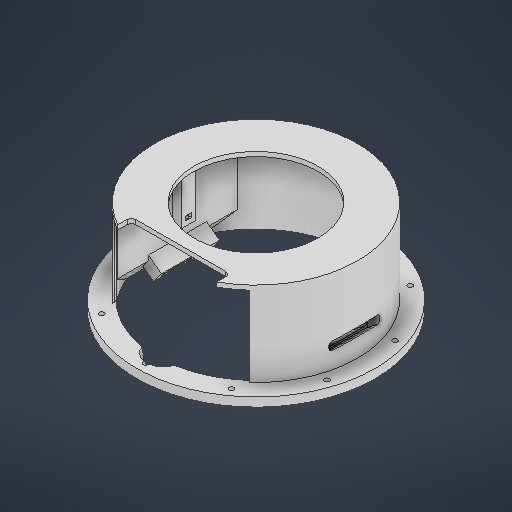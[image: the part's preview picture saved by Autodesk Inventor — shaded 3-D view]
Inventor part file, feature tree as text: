
AUTODESK INVENTOR PART (.ipt)
format: ipt  version: 2025 (Build 290162000, 162)  size: 523,264 bytes
history: native  units: in
note: dims shown in document units (in); Inventor stores cm internally (conversion verified against a paired STEP export)
features: extrude x17, sketch x15, plane x3, fillet x1, chamfer x1
ambient origin geometry x8: Origin, YZ Plane, XZ Plane, XY Plane, X Axis, Y Axis, Z Axis, Center Point
bodies: Solid1 (feature_tree)
feature tree (37):
  sketch  "Sketch1"  dims[d5=0.0in d7=0.0in]
  extrude  "Extrusion1"  TaperAngle=0.0deg  [1 undecoded]
  extrude  "Extrusion2"  Depth=4.5276in
  extrude  "Extrusion7"  Depth=0.2165in
  extrude  "Extrusion34"  Depth=6.1024in
  sketch  "Sketch30"  dims[d272=3.937in d273=4.1535in d274=0.0in d285=3.937in]
  plane  "Work Plane19"
  plane  "Work Plane21"
  plane  "Work Plane22"
  extrude  "Extrusion36"  Depth=4.1535in TaperAngle=0.0deg
  fillet  "Fillet19"  Radius=3.937in
  extrude  "Extrusion37"  Depth=2.0812in TaperAngle=0.0deg
  extrude  "Extrusion38"  Depth=0.1969in
  sketch  "Sketch35"  dims[d293=0.1969in d294=0.1969in]
  extrude  "Extrusion40"  Depth=1.5748in
  extrude  "Extrusion41"  Depth=0.1969in
  extrude  "Extrusion42"  Depth=0.3937in TaperAngle=0.0deg
  extrude  "Extrusion43"  Depth=1.7717in TaperAngle=0.0deg
  chamfer  "Chamfer14"  Distance=0.5906in
  sketch  "Sketch38"  dims[d301=2.9528in]
  extrude  "Extrusion44"  Depth=0.0689in
  extrude  "Extrusion45"  Depth=0.0689in TaperAngle=0.0deg
  sketch  "Sketch39"  dims[d308=6.378in]
  extrude  "Extrusion46"  Depth=0.0689in TaperAngle=0.0deg
  extrude  "Extrusion47"  Depth=0.0689in TaperAngle=0.0deg
  sketch  "Sketch43"  dims[d312=6.8898in d313=5.5413in d314=0.2362in d315=0.1969in d316=0.0in d317=0.1969in d318=0.0in d319=1.378in d320=0.0in d321=0.5906in d322=0.7874in d323=45.0deg d324=1.0in d326=0.315in d328=0.0in d329=0.0in d330=0.1772in d331=0.315in d332=0.0in d333=1.0in d334=0.2953in d335=0.1772in d336=0.0in d337=0.0in d338=0.315in d339=0.0in d340=0.8661in d341=0.8661in d344=0.5906in d345=0.5906in d346=0.5906in d347=0.5906in d348=0.5906in d349=0.0in d350=0.1969in d351=0.0in d352=0.5906in d353=0.5906in d354=0.5906in d355=0.5906in d356=0.5906in d357=0.1969in d358=0.0in d359=0.0in d360=0.0in d361=0.0689in d113=0.0197in d114=0.0344in d115=0.0197in d116=0.0344in d167=0.0197in d168=0.0344in d169=0.0197in d170=0.0344in d215=0.0197in d216=0.0344in d217=0.0197in d218=0.0344in d219=0.0in d220=0.0in d254=0.0197in d255=0.0344in d256=0.0197in d257=0.0344in]
  extrude  "Extrusion49"  Depth=0.5906in TaperAngle=45.0deg
  extrude  "Extrusion50"  Depth=0.0689in
  sketch  "Sketch2"  dims[d18=0.0in d52=4.5276in]
  sketch  "Sketch Circular Pattern5"  dims[d264=9.8425in d265=0.2165in]
  sketch  "Sketch28"  dims[d266=3.937in d268=360.0deg d271=6.1024in]
  sketch  "Sketch31"  dims[d286=1.5748in d287=2.0812in d288=0.0in]
  sketch  "Sketch32"  dims[d289=3.5039in d290=0.1969in]
  sketch  "Sketch33"  dims[d291=4.4094in d292=1.5748in]
  sketch  "Sketch36"  dims[d295=3.3465in d296=0.3937in d297=0.0in]
  sketch  "Sketch37"  dims[d298=0.6299in d299=1.7717in d300=0.0in]
  sketch  "Sketch42"  dims[d309=0.2805in d310=0.5906in d311=0.0in]
note: 1 required parameter value undecoded (feature->parameter linkage not recoverable at this tier; creation-order binding heuristic only, values carry confidence <= 0.55)
